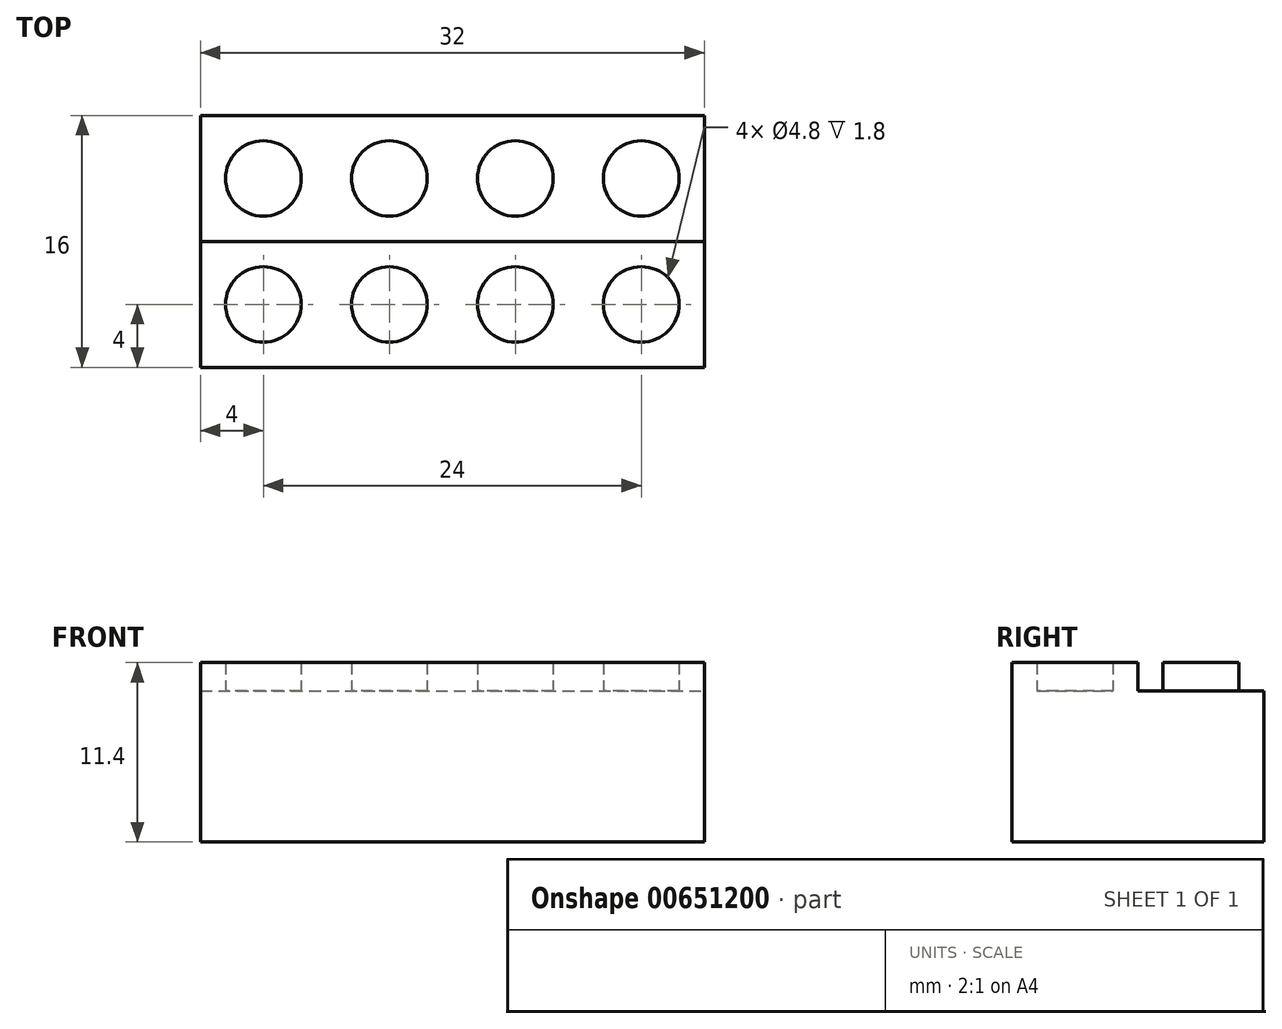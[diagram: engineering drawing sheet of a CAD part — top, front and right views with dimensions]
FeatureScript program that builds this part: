
annotation { "Feature Type Name" : "Feature", "Feature Type Description" : "" }
export const myFeature = defineFeature(function(context is Context, id is Id, definition is map)
    precondition{}
    {
        {
            var Q0;
            Q0=qCreatedBy(makeId("Top.planeOp"),FACE);
            var sketch = newSketch(context, id + "F0", { "sketchPlane" : qUnion([Q0])});
            skLineSegment(sketch, "E0.bottom", {"start": v(0, 0) * mm, "end": v(-32, 0) * mm});
            skLineSegment(sketch, "E0.top", {"start": v(0, 16) * mm, "end": v(-32, 16) * mm});
            skLineSegment(sketch, "E0.left", {"start": v(0, 0) * mm, "end": v(0, 16) * mm});
            skLineSegment(sketch, "E0.right", {"start": v(-32, 0) * mm, "end": v(-32, 16) * mm});
            skSolve(sketch);
        }
        {
            var Q0;
            Q0=makeQuery(id+"F0.imprint","IMPRINT",FACE,{"disambiguationData":[TD([[makeQuery(id+"F0.imprint","IMPRINT",EDGE,{"derivedFrom":sQuery(id+"F0.wireOp",EDGE,"E0.bottom")}),-1.0]])]});
            extrude(context, id + "F1", {"entities" : qUnion([Q0]), "depth" : 9.6 * mm, "offsetDistance" : 25.4 * mm});
        }
        {
            var Q0;
            Q0=makeQuery(id+"F1.opExtrude","CAP_FACE",FACE,{"disambiguationData":[OSD([sQuery(id+"F0.wireOp",EDGE,"E0.bottom"),sQuery(id+"F0.wireOp",EDGE,"E0.top"),sQuery(id+"F0.wireOp",EDGE,"E0.left"),sQuery(id+"F0.wireOp",EDGE,"E0.right")])],"isStart":false});
            var sketch = newSketch(context, id + "F2", { "sketchPlane" : qUnion([Q0])});
            skLineSegment(sketch, "E1", {"start": v(-32, 8) * mm, "end": v(0, 8) * mm});
            skLineSegment(sketch, "E2", {"start": v(-24, 16) * mm, "end": v(-24, 0) * mm});
            skLineSegment(sketch, "E3", {"start": v(-16, 16) * mm, "end": v(-16, 0) * mm});
            skLineSegment(sketch, "E4", {"start": v(-8, 16) * mm, "end": v(-8, 0) * mm});
            skLineSegment(sketch, "E5", {"start": v(-32, 16) * mm, "end": v(-24, 8) * mm});
            skLineSegment(sketch, "E6", {"start": v(-24, 8) * mm, "end": v(-16, 16) * mm});
            skLineSegment(sketch, "E7", {"start": v(-16, 16) * mm, "end": v(-8, 8) * mm});
            skLineSegment(sketch, "E8", {"start": v(-8, 8) * mm, "end": v(0, 16) * mm});
            skCircle(sketch, "E9", {"center": v(-28, 12) * mm, "radius": 2.4 * mm});
            skCircle(sketch, "E10", {"center": v(-20, 12) * mm, "radius": 2.4 * mm});
            skCircle(sketch, "E11", {"center": v(-12, 12) * mm, "radius": 2.4 * mm});
            skCircle(sketch, "E12", {"center": v(-4, 12) * mm, "radius": 2.4 * mm});
            skCircle(sketch, "E13.MirrorC", {"center": v(-28, 4) * mm, "radius": 2.4 * mm});
            skCircle(sketch, "E14.MirrorC", {"center": v(-20, 4) * mm, "radius": 2.4 * mm});
            skCircle(sketch, "E15.MirrorC", {"center": v(-12, 4) * mm, "radius": 2.4 * mm});
            skCircle(sketch, "E16.MirrorC", {"center": v(-4, 4) * mm, "radius": 2.4 * mm});
            skSolve(sketch);
        }
        {
            var Q0;
            {var subQ0=sQuery(id+"F2.wireOp",EDGE,"E9");var subQ1=sQuery(id+"F2.wireOp",EDGE,"E5");var subQ2=makeQuery(id+"F2.imprint","INTERSECT",VERTEX,{"disambiguationData":[OD(0.0)],"derivedFrom":[subQ1,subQ0]});Q0=makeQuery(id+"F2.imprint","IMPRINT",FACE,{"disambiguationData":[TD([[makeQuery(id+"F2.imprint","IMPRINT",EDGE,{"disambiguationData":[TD([[subQ2,-1.0]])],"derivedFrom":subQ1}),-1.0]])]});}
            var Q1;
            {var subQ0=sQuery(id+"F2.wireOp",EDGE,"E9");var subQ1=sQuery(id+"F2.wireOp",EDGE,"E5");var subQ2=makeQuery(id+"F2.imprint","INTERSECT",VERTEX,{"disambiguationData":[OD(0.0)],"derivedFrom":[subQ1,subQ0]});Q1=makeQuery(id+"F2.imprint","IMPRINT",FACE,{"disambiguationData":[TD([[makeQuery(id+"F2.imprint","IMPRINT",EDGE,{"disambiguationData":[TD([[subQ2,-1.0]])],"derivedFrom":subQ1}),1.0]])]});}
            var Q2;
            {var subQ0=sQuery(id+"F2.wireOp",EDGE,"E10");var subQ1=sQuery(id+"F2.wireOp",EDGE,"E6");var subQ2=makeQuery(id+"F2.imprint","INTERSECT",VERTEX,{"disambiguationData":[OD(0.0)],"derivedFrom":[subQ1,subQ0]});Q2=makeQuery(id+"F2.imprint","IMPRINT",FACE,{"disambiguationData":[TD([[makeQuery(id+"F2.imprint","IMPRINT",EDGE,{"disambiguationData":[TD([[subQ2,-1.0]])],"derivedFrom":subQ1}),1.0]])]});}
            var Q3;
            {var subQ0=sQuery(id+"F2.wireOp",EDGE,"E10");var subQ1=sQuery(id+"F2.wireOp",EDGE,"E6");var subQ2=makeQuery(id+"F2.imprint","INTERSECT",VERTEX,{"disambiguationData":[OD(0.0)],"derivedFrom":[subQ1,subQ0]});Q3=makeQuery(id+"F2.imprint","IMPRINT",FACE,{"disambiguationData":[TD([[makeQuery(id+"F2.imprint","IMPRINT",EDGE,{"disambiguationData":[TD([[subQ2,-1.0]])],"derivedFrom":subQ1}),-1.0]])]});}
            var Q4;
            {var subQ0=sQuery(id+"F2.wireOp",EDGE,"E11");var subQ1=sQuery(id+"F2.wireOp",EDGE,"E7");var subQ2=makeQuery(id+"F2.imprint","INTERSECT",VERTEX,{"disambiguationData":[OD(0.0)],"derivedFrom":[subQ1,subQ0]});Q4=makeQuery(id+"F2.imprint","IMPRINT",FACE,{"disambiguationData":[TD([[makeQuery(id+"F2.imprint","IMPRINT",EDGE,{"disambiguationData":[TD([[subQ2,-1.0]])],"derivedFrom":subQ1}),-1.0]])]});}
            var Q5;
            {var subQ0=sQuery(id+"F2.wireOp",EDGE,"E11");var subQ1=sQuery(id+"F2.wireOp",EDGE,"E7");var subQ2=makeQuery(id+"F2.imprint","INTERSECT",VERTEX,{"disambiguationData":[OD(0.0)],"derivedFrom":[subQ1,subQ0]});Q5=makeQuery(id+"F2.imprint","IMPRINT",FACE,{"disambiguationData":[TD([[makeQuery(id+"F2.imprint","IMPRINT",EDGE,{"disambiguationData":[TD([[subQ2,-1.0]])],"derivedFrom":subQ1}),1.0]])]});}
            var Q6;
            {var subQ0=sQuery(id+"F2.wireOp",EDGE,"E12");var subQ1=sQuery(id+"F2.wireOp",EDGE,"E8");var subQ2=makeQuery(id+"F2.imprint","INTERSECT",VERTEX,{"disambiguationData":[OD(0.0)],"derivedFrom":[subQ1,subQ0]});Q6=makeQuery(id+"F2.imprint","IMPRINT",FACE,{"disambiguationData":[TD([[makeQuery(id+"F2.imprint","IMPRINT",EDGE,{"disambiguationData":[TD([[subQ2,-1.0]])],"derivedFrom":subQ1}),1.0]])]});}
            var Q7;
            {var subQ0=sQuery(id+"F2.wireOp",EDGE,"E12");var subQ1=sQuery(id+"F2.wireOp",EDGE,"E8");var subQ2=makeQuery(id+"F2.imprint","INTERSECT",VERTEX,{"disambiguationData":[OD(0.0)],"derivedFrom":[subQ1,subQ0]});Q7=makeQuery(id+"F2.imprint","IMPRINT",FACE,{"disambiguationData":[TD([[makeQuery(id+"F2.imprint","IMPRINT",EDGE,{"disambiguationData":[TD([[subQ2,-1.0]])],"derivedFrom":subQ1}),-1.0]])]});}
            var Q8;
            Q8=makeQuery(id+"F2.imprint","IMPRINT",FACE,{"disambiguationData":[TD([[makeQuery(id+"F2.imprint","IMPRINT",EDGE,{"derivedFrom":sQuery(id+"F2.wireOp",EDGE,"E16.MirrorC")}),-1.0]])]});
            var Q9;
            Q9=makeQuery(id+"F2.imprint","IMPRINT",FACE,{"disambiguationData":[TD([[makeQuery(id+"F2.imprint","IMPRINT",EDGE,{"derivedFrom":sQuery(id+"F2.wireOp",EDGE,"E15.MirrorC")}),-1.0]])]});
            var Q10;
            Q10=makeQuery(id+"F2.imprint","IMPRINT",FACE,{"disambiguationData":[TD([[makeQuery(id+"F2.imprint","IMPRINT",EDGE,{"derivedFrom":sQuery(id+"F2.wireOp",EDGE,"E14.MirrorC")}),-1.0]])]});
            var Q11;
            Q11=makeQuery(id+"F2.imprint","IMPRINT",FACE,{"disambiguationData":[TD([[makeQuery(id+"F2.imprint","IMPRINT",EDGE,{"derivedFrom":sQuery(id+"F2.wireOp",EDGE,"E13.MirrorC")}),-1.0]])]});
            extrude(context, id + "F3", {"entities" : qUnion([Q0, Q1, Q2, Q3, Q4, Q5, Q6, Q7, Q8, Q9, Q10, Q11]), "operationType" : NewBodyOperationType.ADD, "depth" : 1.8 * mm, "offsetDistance" : 25.4 * mm});
        }
    });
